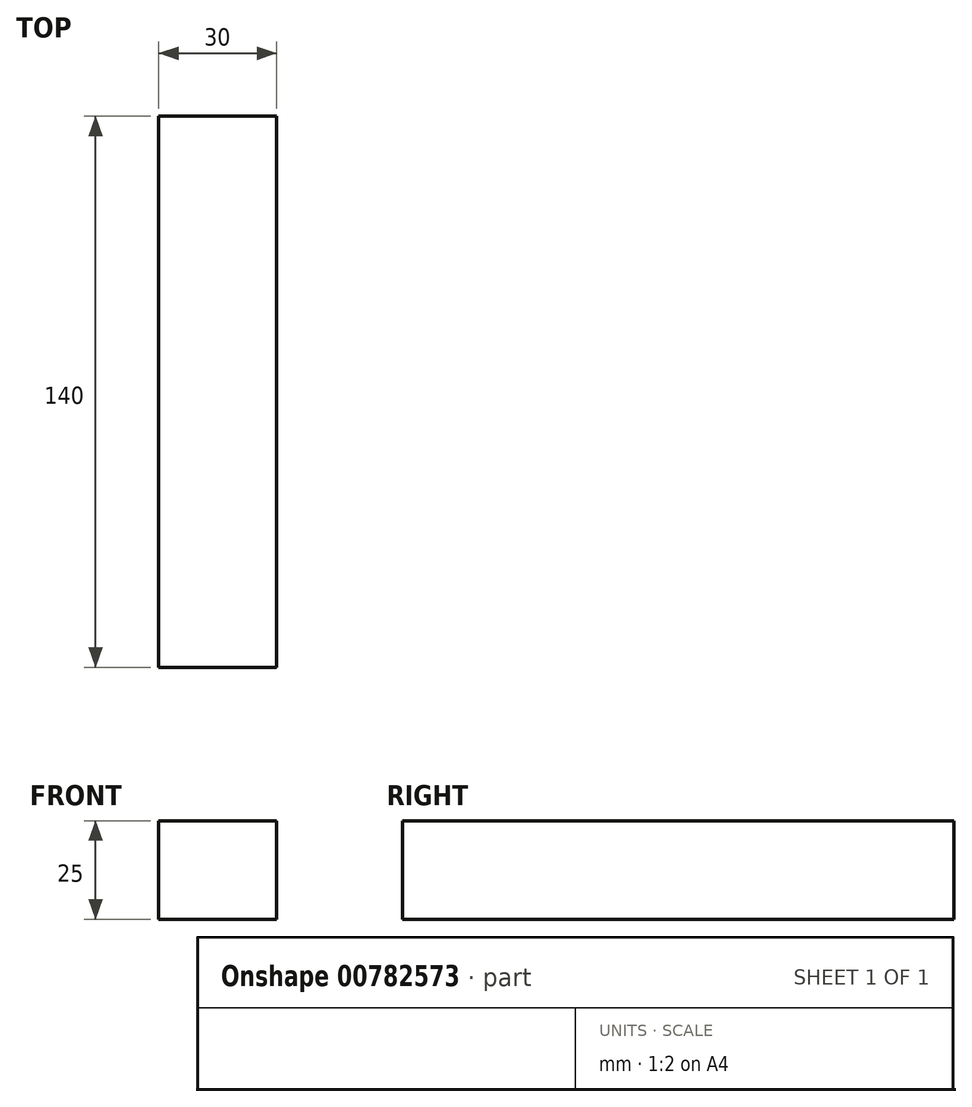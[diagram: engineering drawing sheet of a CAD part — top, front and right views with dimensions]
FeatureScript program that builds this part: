
annotation { "Feature Type Name" : "Feature", "Feature Type Description" : "" }
export const myFeature = defineFeature(function(context is Context, id is Id, definition is map)
    precondition{}
    {
        {
            var Q0;
            Q0=qCreatedBy(makeId("Top.planeOp"),FACE);
            var sketch = newSketch(context, id + "F0", { "sketchPlane" : qUnion([Q0])});
            skLineSegment(sketch, "E0.bottom", {"start": v(15, -70) * mm, "end": v(-15, -70) * mm});
            skLineSegment(sketch, "E0.top", {"start": v(15, 70) * mm, "end": v(-15, 70) * mm});
            skLineSegment(sketch, "E0.left", {"start": v(15, -70) * mm, "end": v(15, 70) * mm});
            skLineSegment(sketch, "E0.right", {"start": v(-15, -70) * mm, "end": v(-15, 70) * mm});
            skPoint(sketch, "E0.middle", {"position": v(0, 0) * mm});
            skSolve(sketch);
        }
        {
            var Q0;
            Q0 = qSketchRegion(id + "F0", true);
            extrude(context, id + "F1", {"entities" : qUnion([Q0]), "depth" : 25 * mm, "offsetDistance" : 25 * mm});
        }
    });
